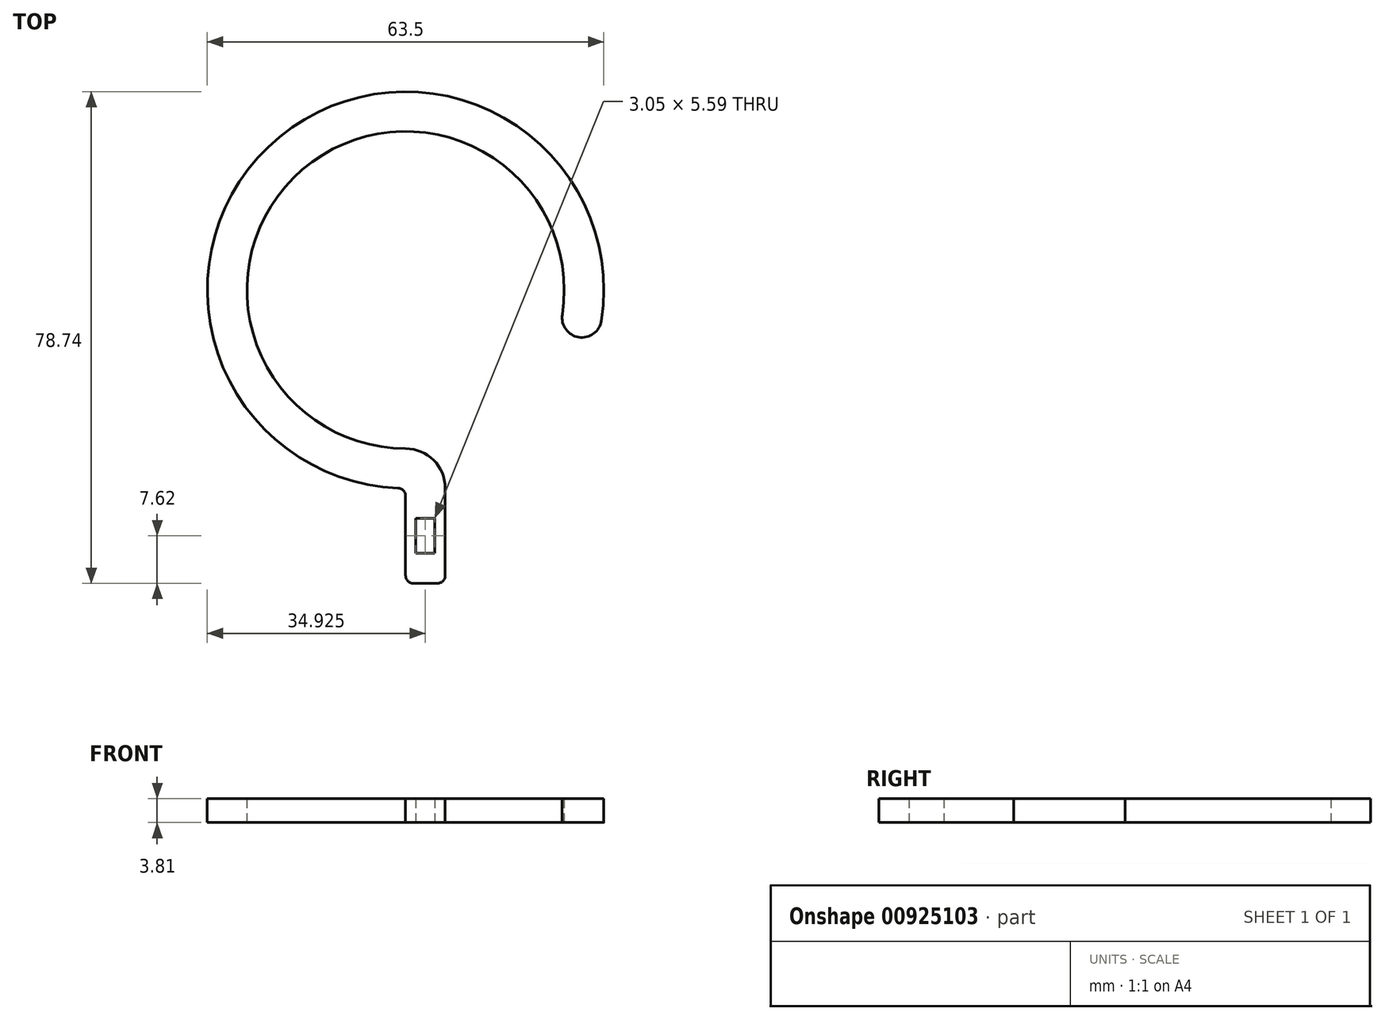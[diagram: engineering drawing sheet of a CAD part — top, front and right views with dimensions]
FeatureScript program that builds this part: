
annotation { "Feature Type Name" : "Feature", "Feature Type Description" : "" }
export const myFeature = defineFeature(function(context is Context, id is Id, definition is map)
    precondition{}
    {
        {
            var Q0;
            Q0=qCreatedBy(makeId("Top.planeOp"),FACE);
            var sketch = newSketch(context, id + "F0", { "sketchPlane" : qUnion([Q0])});
            skArc(sketch, "E0", {"start": v(25.1, -3.94) * mm, "mid": v(-16.51, 19.3) * mm, "end": v(0, -25.4) * mm});
            skArc(sketch, "E1.0", {"start": v(31.37, -4.92) * mm, "mid": v(-20.17, 24.52) * mm, "end": v(-1.22, -31.73) * mm});
            skArc(sketch, "E2", {"start": v(25.1, -3.94) * mm, "mid": v(27.74, -7.57) * mm, "end": v(31.37, -4.92) * mm});
            skArc(sketch, "E3", {"start": v(0, -25.4) * mm, "mid": v(4.5, -27.26) * mm, "end": v(6.35, -31.75) * mm});
            skLineSegment(sketch, "E4", {"start": v(0, -31.75) * mm, "end": v(12.7, -31.75) * mm, "construction": true});
            skLineSegment(sketch, "E5.bottom", {"start": v(0, -31.75) * mm, "end": v(6.35, -31.75) * mm});
            skLineSegment(sketch, "E5.top", {"start": v(1.27, -47) * mm, "end": v(5.08, -47) * mm});
            skLineSegment(sketch, "E5.left", {"start": v(0, -33) * mm, "end": v(0, -45.72) * mm});
            skLineSegment(sketch, "E5.right", {"start": v(6.35, -31.75) * mm, "end": v(6.35, -45.72) * mm});
            skLineSegment(sketch, "E6.bottom", {"start": v(1.65, -36.58) * mm, "end": v(4.7, -36.58) * mm});
            skLineSegment(sketch, "E6.top", {"start": v(1.65, -42.16) * mm, "end": v(4.7, -42.16) * mm});
            skLineSegment(sketch, "E6.left", {"start": v(1.65, -36.58) * mm, "end": v(1.65, -42.16) * mm});
            skLineSegment(sketch, "E6.right", {"start": v(4.7, -36.58) * mm, "end": v(4.7, -42.16) * mm});
            skArc(sketch, "E7.filletArc", {"start": v(0, -33) * mm, "mid": v(-0.35, -32.11) * mm, "end": v(-1.22, -31.73) * mm});
            skLineSegment(sketch, "E8", {"start": v(25.1, -3.94) * mm, "end": v(31.37, -4.92) * mm, "construction": true});
            skPoint(sketch, "E9.visualSharp", {"position": v(0, -47) * mm});
            skArc(sketch, "E9.filletArc", {"start": v(0, -45.72) * mm, "mid": v(0.37, -46.62) * mm, "end": v(1.27, -47) * mm});
            skPoint(sketch, "E10.visualSharp", {"position": v(6.35, -47) * mm});
            skArc(sketch, "E10.filletArc", {"start": v(5.08, -47) * mm, "mid": v(5.98, -46.62) * mm, "end": v(6.35, -45.72) * mm});
            skSolve(sketch);
        }
        {
            var Q0;
            Q0 = qSketchRegion(id + "F0", true);
            extrude(context, id + "F1", {"entities" : qUnion([Q0]), "depth" : 3.8 * mm, "offsetDistance" : 25.4 * mm});
        }
    });
